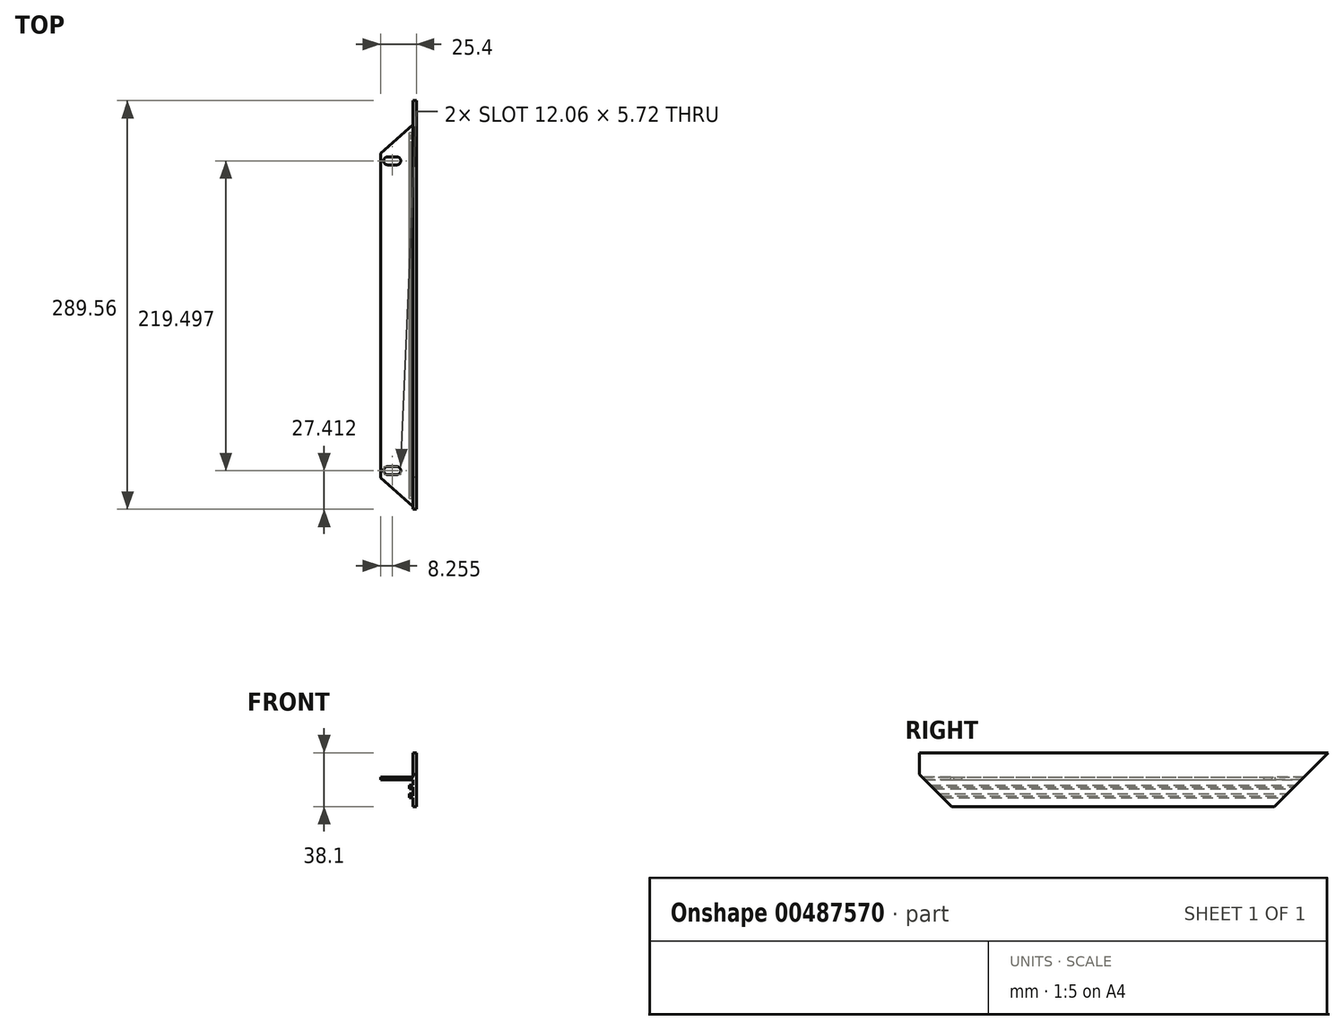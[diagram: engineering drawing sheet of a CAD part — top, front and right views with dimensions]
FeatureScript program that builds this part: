
annotation { "Feature Type Name" : "Feature", "Feature Type Description" : "" }
export const myFeature = defineFeature(function(context is Context, id is Id, definition is map)
    precondition{}
    {
        {
            var Q0;
            Q0=qCreatedBy(makeId("Front.planeOp"),FACE);
            var sketch = newSketch(context, id + "F0", { "sketchPlane" : qUnion([Q0])});
            skLineSegment(sketch, "E0", {"start": v(0, 0) * mm, "end": v(0, 38.1) * mm});
            skLineSegment(sketch, "E1", {"start": v(0, 38.1) * mm, "end": v(-2.54, 38.1) * mm});
            skLineSegment(sketch, "E2", {"start": v(-2.54, 38.1) * mm, "end": v(-2.54, 20.96) * mm});
            skLineSegment(sketch, "E3", {"start": v(-2.54, 20.96) * mm, "end": v(-25.4, 20.95) * mm});
            skLineSegment(sketch, "E4", {"start": v(-25.4, 20.95) * mm, "end": v(-25.4, 19.05) * mm});
            skLineSegment(sketch, "E5", {"start": v(-25.4, 19.05) * mm, "end": v(-2.54, 19.05) * mm});
            skLineSegment(sketch, "E6", {"start": v(-2.54, 6.35) * mm, "end": v(-2.54, 0) * mm});
            skLineSegment(sketch, "E7", {"start": v(-2.54, 0) * mm, "end": v(0, 0) * mm});
            skLineSegment(sketch, "E8", {"start": v(-5.08, 15.24) * mm, "end": v(-5.08, 12.45) * mm});
            skLineSegment(sketch, "E9", {"start": v(-5.08, 6.35) * mm, "end": v(-2.54, 6.35) * mm});
            skLineSegment(sketch, "E10.bottom", {"start": v(-3.8, 7.62) * mm, "end": v(-2.54, 7.62) * mm});
            skLineSegment(sketch, "E10.top", {"start": v(-3.81, 13.97) * mm, "end": v(-2.54, 13.97) * mm});
            skLineSegment(sketch, "E10.left", {"start": v(-3.8, 7.62) * mm, "end": v(-3.8, 9.14) * mm});
            skLineSegment(sketch, "E10.right", {"start": v(-2.54, 7.62) * mm, "end": v(-2.54, 13.97) * mm});
            skLineSegment(sketch, "E11", {"start": v(-5.08, 15.24) * mm, "end": v(-2.54, 15.24) * mm});
            skLineSegment(sketch, "E12", {"start": v(-2.54, 15.24) * mm, "end": v(-2.54, 19.05) * mm});
            skLineSegment(sketch, "E13", {"start": v(-5.08, 12.45) * mm, "end": v(-3.81, 12.45) * mm});
            skLineSegment(sketch, "E14", {"start": v(-3.8, 9.14) * mm, "end": v(-5.08, 9.14) * mm});
            skLineSegment(sketch, "E15.trimOffspring", {"start": v(-5.08, 9.14) * mm, "end": v(-5.08, 6.35) * mm});
            skLineSegment(sketch, "E16.trimOffspring", {"start": v(-3.81, 12.45) * mm, "end": v(-3.81, 13.97) * mm});
            skSolve(sketch);
        }
        {
            var Q0;
            Q0=makeQuery(id+"F0.imprint","IMPRINT",FACE,{"disambiguationData":[TD([[makeQuery(id+"F0.imprint","IMPRINT",EDGE,{"derivedFrom":sQuery(id+"F0.wireOp",EDGE,"E0")}),1.0]])]});
            extrude(context, id + "F1", {"entities" : qUnion([Q0]), "depth" : 304.8 * mm});
        }
        {
            var Q0;
            Q0=makeQuery(id+"F1.opExtrude","SWEPT_FACE",FACE,{"disambiguationData":[OSD([sQuery(id+"F0.wireOp",EDGE,"E0")])]});
            var sketch = newSketch(context, id + "F2", { "sketchPlane" : qUnion([Q0])});
            skLineSegment(sketch, "E17", {"start": v(-304.8, 38.1) * mm, "end": v(-266.7, 0) * mm});
            skLineSegment(sketch, "E18", {"start": v(-266.7, 0) * mm, "end": v(-304.8, 0) * mm});
            skLineSegment(sketch, "E19", {"start": v(-304.8, 0) * mm, "end": v(-304.8, 38.1) * mm});
            skLineSegment(sketch, "E20", {"start": v(0, 38.1) * mm, "end": v(0, 0) * mm});
            skLineSegment(sketch, "E21", {"start": v(0, 0) * mm, "end": v(-38.1, 0) * mm});
            skLineSegment(sketch, "E22", {"start": v(-38.1, 0) * mm, "end": v(0, 38.1) * mm});
            skSolve(sketch);
        }
        {
            var Q0;
            Q0 = qSketchRegion(id + "F2", true);
            extrude(context, id + "F3", {"entities" : qUnion([Q0]), "operationType" : NewBodyOperationType.REMOVE, "oppositeDirection" : true, "depth" : 25.4 * mm});
        }
        {
            var Q0;
            Q0=makeQuery(id+"F1.opExtrude","SWEPT_FACE",FACE,{"disambiguationData":[OSD([sQuery(id+"F0.wireOp",EDGE,"E3")])]});
            var sketch = newSketch(context, id + "F4", { "sketchPlane" : qUnion([Q0])});
            skLineSegment(sketch, "E23", {"start": v(-2.54, -17.15) * mm, "end": v(-25.4, -37.47) * mm});
            skLineSegment(sketch, "E24", {"start": v(-25.4, -37.47) * mm, "end": v(-25.4, -17.15) * mm});
            skLineSegment(sketch, "E25", {"start": v(-25.4, -17.15) * mm, "end": v(-2.54, -17.15) * mm});
            skLineSegment(sketch, "E26", {"start": v(-2.54, -287.66) * mm, "end": v(-25.4, -287.66) * mm});
            skLineSegment(sketch, "E27", {"start": v(-25.4, -287.66) * mm, "end": v(-25.4, -267.34) * mm});
            skLineSegment(sketch, "E28", {"start": v(-25.4, -267.34) * mm, "end": v(-2.54, -287.66) * mm});
            skSolve(sketch);
        }
        {
            var Q0;
            Q0 = qSketchRegion(id + "F4", true);
            extrude(context, id + "F5", {"entities" : qUnion([Q0]), "operationType" : NewBodyOperationType.REMOVE, "oppositeDirection" : true, "depth" : 25.4 * mm});
        }
        {
            var Q0;
            Q0=makeQuery(id+"F1.opExtrude","SWEPT_FACE",FACE,{"disambiguationData":[OSD([sQuery(id+"F0.wireOp",EDGE,"E3")])]});
            var sketch = newSketch(context, id + "F6", { "sketchPlane" : qUnion([Q0])});
            skLineSegment(sketch, "E29", {"start": v(-25.4, -37.47) * mm, "end": v(-2.54, -37.47) * mm, "construction": true});
            skLineSegment(sketch, "E30", {"start": v(-2.54, -37.47) * mm, "end": v(-13.97, -27.3) * mm, "construction": true});
            skLineSegment(sketch, "E31", {"start": v(-13.97, -27.3) * mm, "end": v(-25.4, -37.47) * mm, "construction": true});
            skLineSegment(sketch, "E32", {"start": v(-20.32, -39.8) * mm, "end": v(-13.97, -39.8) * mm});
            skLineSegment(sketch, "E33", {"start": v(-20.32, -45.5) * mm, "end": v(-13.97, -45.5) * mm});
            skArc(sketch, "E34", {"start": v(-20.32, -39.8) * mm, "mid": v(-23.18, -42.65) * mm, "end": v(-20.32, -45.5) * mm});
            skArc(sketch, "E35", {"start": v(-13.97, -39.8) * mm, "mid": v(-11.11, -42.65) * mm, "end": v(-13.97, -45.5) * mm});
            skLineSegment(sketch, "E36", {"start": v(-2.54, -152.4) * mm, "end": v(-25.4, -152.4) * mm, "construction": true});
            skArc(sketch, "E37.MirrorCS", {"start": v(-13.97, -265) * mm, "mid": v(-11.11, -262.15) * mm, "end": v(-13.97, -259.3) * mm});
            skArc(sketch, "E38.MirrorCS", {"start": v(-20.32, -265) * mm, "mid": v(-23.18, -262.15) * mm, "end": v(-20.32, -259.3) * mm});
            skLineSegment(sketch, "E39.MirrorCS", {"start": v(-20.32, -259.3) * mm, "end": v(-13.97, -259.3) * mm});
            skLineSegment(sketch, "E40.MirrorCS", {"start": v(-25.4, -267.34) * mm, "end": v(-2.54, -267.34) * mm, "construction": true});
            skLineSegment(sketch, "E41.MirrorCS", {"start": v(-2.54, -267.33) * mm, "end": v(-13.97, -277.5) * mm, "construction": true});
            skLineSegment(sketch, "E42.MirrorCS", {"start": v(-13.97, -277.5) * mm, "end": v(-25.4, -267.34) * mm, "construction": true});
            skLineSegment(sketch, "E43.MirrorCS", {"start": v(-20.32, -265) * mm, "end": v(-13.97, -265) * mm});
            skSolve(sketch);
        }
        {
            var Q0;
            Q0 = qSketchRegion(id + "F6", true);
            extrude(context, id + "F7", {"entities" : qUnion([Q0]), "operationType" : NewBodyOperationType.REMOVE, "oppositeDirection" : true, "depth" : 25.4 * mm});
        }
        {
            var Q0;
            Q0=makeQuery(id+"F1.opExtrude","SWEPT_FACE",FACE,{"disambiguationData":[OSD([sQuery(id+"F0.wireOp",EDGE,"E0")])]});
            var sketch = newSketch(context, id + "F8", { "sketchPlane" : qUnion([Q0])});
            skLineSegment(sketch, "E44", {"start": v(-289.56, 38.1) * mm, "end": v(-289.56, 22.86) * mm});
            skLineSegment(sketch, "E45", {"start": v(-289.56, 22.86) * mm, "end": v(-304.8, 38.1) * mm});
            skLineSegment(sketch, "E46", {"start": v(-304.8, 38.1) * mm, "end": v(-289.56, 38.1) * mm});
            skSolve(sketch);
        }
        {
            var Q0;
            Q0 = qSketchRegion(id + "F8", true);
            extrude(context, id + "F9", {"entities" : qUnion([Q0]), "operationType" : NewBodyOperationType.REMOVE, "oppositeDirection" : true, "depth" : 25.4 * mm});
        }
    });
